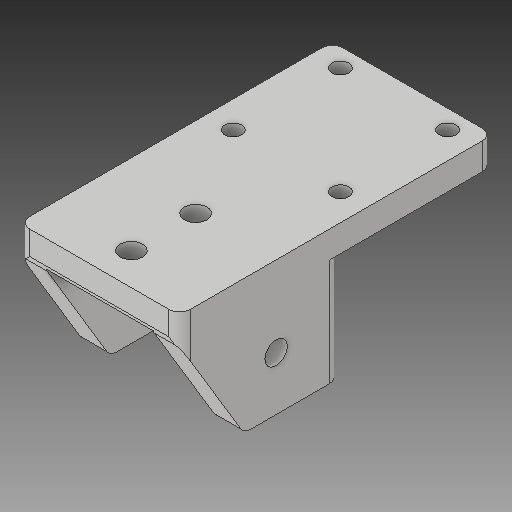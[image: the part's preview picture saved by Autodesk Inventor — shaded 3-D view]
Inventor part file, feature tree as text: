
AUTODESK INVENTOR PART (.ipt)
format: ipt  version: 2018 (Build 220112000, 112)  size: 143,872 bytes
history: native  units: in
note: dims shown in document units (in); Inventor stores cm internally (conversion verified against a paired STEP export)
features: sketch x6, other x3
ambient origin geometry x8: Origin, YZ Plane, XZ Plane, XY Plane, X Axis, Y Axis, Z Axis, Center Point
bodies: Solid1 (feature_tree)
feature tree (9):
  other  "X-connectorLeft.ipt"
  other  "Solid1::X-connectorLeft.ipt"
  other  "TaggingFeature1"
  sketch  "Sketch1"  dims[d0=0.3937in]
  sketch  "Sketch2"
  sketch  "Sketch3"
  sketch  "Sketch4"
  sketch  "Sketch5"
  sketch  "Sketch6"
